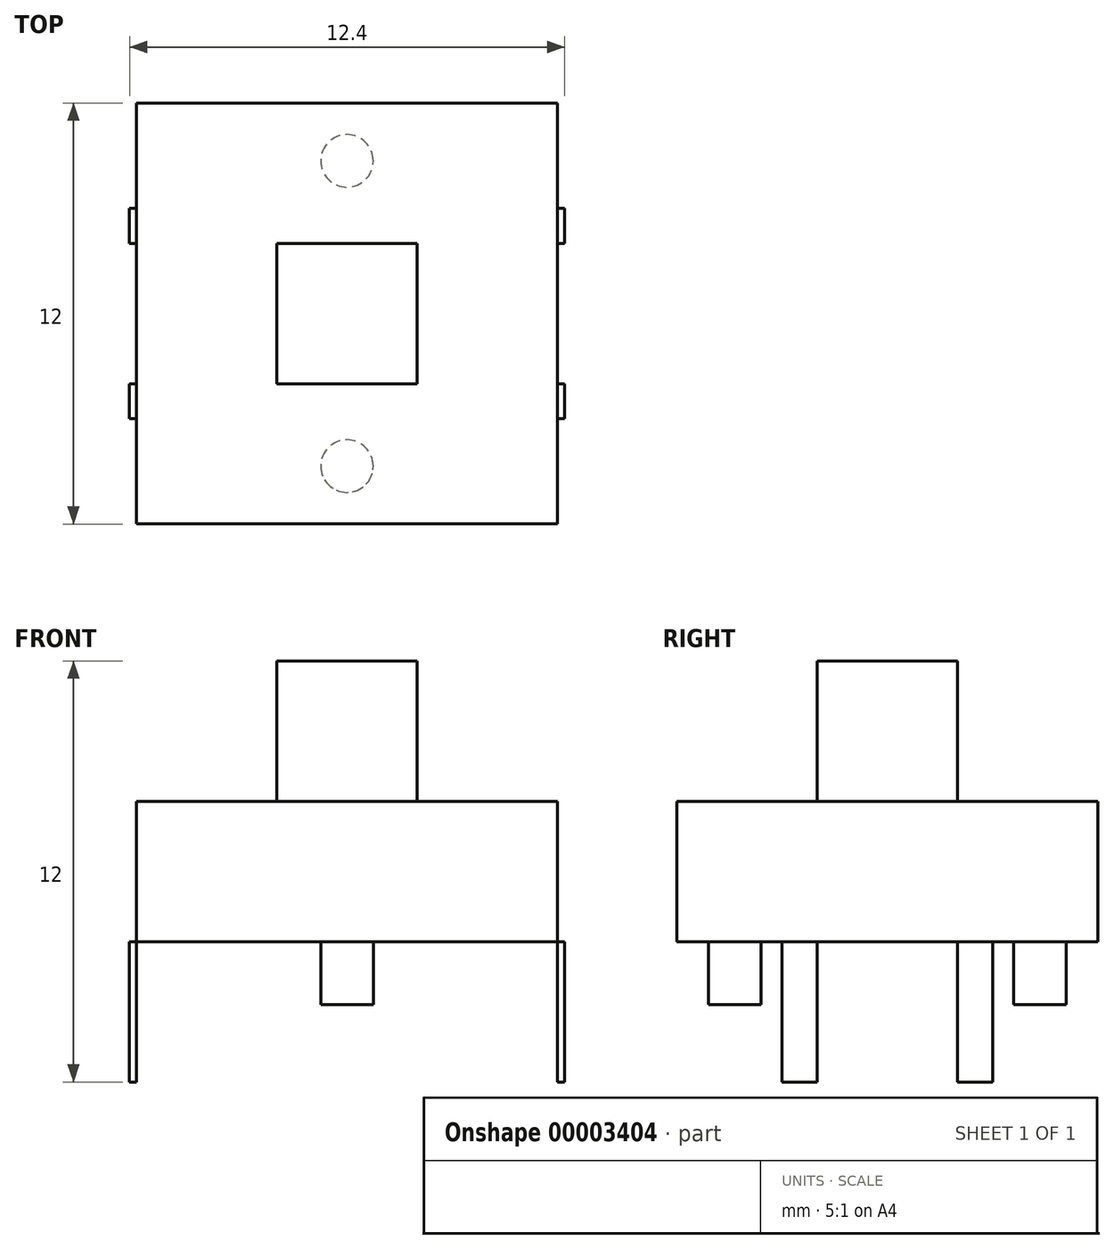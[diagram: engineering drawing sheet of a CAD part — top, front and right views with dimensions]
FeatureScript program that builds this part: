
annotation { "Feature Type Name" : "Feature", "Feature Type Description" : "" }
export const myFeature = defineFeature(function(context is Context, id is Id, definition is map)
    precondition{}
    {
        {
            var Q0;
            Q0=qCreatedBy(makeId("Top.planeOp"),FACE);
            var sketch = newSketch(context, id + "F0", { "sketchPlane" : qUnion([Q0])});
            skLineSegment(sketch, "E0.bottom", {"start": v(-5.22, 9.33) * mm, "end": v(6.78, 9.33) * mm});
            skLineSegment(sketch, "E0.top", {"start": v(-5.22, -2.67) * mm, "end": v(6.78, -2.67) * mm});
            skLineSegment(sketch, "E0.left", {"start": v(-5.22, 9.33) * mm, "end": v(-5.22, -2.67) * mm});
            skLineSegment(sketch, "E0.right", {"start": v(6.78, 9.33) * mm, "end": v(6.78, -2.67) * mm});
            skSolve(sketch);
        }
        {
            var Q0;
            Q0=makeQuery(id+"F0.imprint","IMPRINT",FACE,{"disambiguationData":[TD([[makeQuery(id+"F0.imprint","IMPRINT",EDGE,{"derivedFrom":sQuery(id+"F0.wireOp",EDGE,"E0.bottom")}),-1.0]])]});
            extrude(context, id + "F1", {"entities" : qUnion([Q0]), "depth" : 4 * mm});
        }
        {
            var Q0;
            Q0=makeQuery(id+"F1.opExtrude","CAP_FACE",FACE,{"disambiguationData":[OSD([sQuery(id+"F0.wireOp",EDGE,"E0.bottom"),sQuery(id+"F0.wireOp",EDGE,"E0.top"),sQuery(id+"F0.wireOp",EDGE,"E0.left"),sQuery(id+"F0.wireOp",EDGE,"E0.right")])],"isStart":false});
            var sketch = newSketch(context, id + "F2", { "sketchPlane" : qUnion([Q0])});
            skLineSegment(sketch, "E1.0.0", {"start": v(-5.22, 9.33) * mm, "end": v(6.78, 9.33) * mm});
            skLineSegment(sketch, "E1.0.1", {"start": v(-5.22, 9.33) * mm, "end": v(-5.22, -2.67) * mm});
            skLineSegment(sketch, "E1.0.2", {"start": v(-5.22, -2.67) * mm, "end": v(6.78, -2.67) * mm});
            skLineSegment(sketch, "E1.0.3", {"start": v(6.78, 9.33) * mm, "end": v(6.78, -2.67) * mm});
            skLineSegment(sketch, "E2.0", {"start": v(-1.22, 5.33) * mm, "end": v(2.78, 5.33) * mm});
            skLineSegment(sketch, "E2.1", {"start": v(-1.22, 5.33) * mm, "end": v(-1.22, 1.33) * mm});
            skLineSegment(sketch, "E2.2", {"start": v(-1.22, 1.33) * mm, "end": v(2.78, 1.33) * mm});
            skLineSegment(sketch, "E2.3", {"start": v(2.78, 5.33) * mm, "end": v(2.78, 1.33) * mm});
            skSolve(sketch);
        }
        {
            var Q0;
            Q0=makeQuery(id+"F2.imprint","IMPRINT",FACE,{"disambiguationData":[TD([[makeQuery(id+"F2.imprint","IMPRINT",EDGE,{"derivedFrom":sQuery(id+"F2.wireOp",EDGE,"E2.0")}),-1.0]])]});
            extrude(context, id + "F3", {"entities" : qUnion([Q0]), "operationType" : NewBodyOperationType.ADD, "depth" : 4 * mm});
        }
        {
            var Q0;
            Q0=makeQuery(id+"F1.opExtrude","CAP_FACE",FACE,{"disambiguationData":[OSD([sQuery(id+"F0.wireOp",EDGE,"E0.bottom"),sQuery(id+"F0.wireOp",EDGE,"E0.top"),sQuery(id+"F0.wireOp",EDGE,"E0.left"),sQuery(id+"F0.wireOp",EDGE,"E0.right")])],"isStart":true});
            var sketch = newSketch(context, id + "F4", { "sketchPlane" : qUnion([Q0])});
            skLineSegment(sketch, "E3.bottom", {"start": v(6.98, -0.33) * mm, "end": v(6.78, -0.33) * mm});
            skLineSegment(sketch, "E3.top", {"start": v(6.98, -1.33) * mm, "end": v(6.78, -1.33) * mm});
            skLineSegment(sketch, "E3.left", {"start": v(6.78, -0.33) * mm, "end": v(6.78, -1.33) * mm});
            skLineSegment(sketch, "E3.right", {"start": v(6.98, -0.33) * mm, "end": v(6.98, -1.33) * mm});
            skLineSegment(sketch, "E4.bottom", {"start": v(6.78, -6.33) * mm, "end": v(6.98, -6.33) * mm});
            skLineSegment(sketch, "E4.top", {"start": v(6.78, -5.33) * mm, "end": v(6.98, -5.33) * mm});
            skLineSegment(sketch, "E4.left", {"start": v(6.78, -6.33) * mm, "end": v(6.78, -5.33) * mm});
            skLineSegment(sketch, "E4.right", {"start": v(6.98, -6.33) * mm, "end": v(6.98, -5.33) * mm});
            skLineSegment(sketch, "E5.bottom", {"start": v(-5.22, -0.33) * mm, "end": v(-5.42, -0.33) * mm});
            skLineSegment(sketch, "E5.top", {"start": v(-5.22, -1.33) * mm, "end": v(-5.42, -1.33) * mm});
            skLineSegment(sketch, "E5.left", {"start": v(-5.22, -0.33) * mm, "end": v(-5.22, -1.33) * mm});
            skLineSegment(sketch, "E5.right", {"start": v(-5.42, -0.33) * mm, "end": v(-5.42, -1.33) * mm});
            skLineSegment(sketch, "E6.bottom", {"start": v(-5.22, -5.33) * mm, "end": v(-5.42, -5.33) * mm});
            skLineSegment(sketch, "E6.top", {"start": v(-5.22, -6.33) * mm, "end": v(-5.42, -6.33) * mm});
            skLineSegment(sketch, "E6.left", {"start": v(-5.22, -5.33) * mm, "end": v(-5.22, -6.33) * mm});
            skLineSegment(sketch, "E6.right", {"start": v(-5.42, -5.33) * mm, "end": v(-5.42, -6.33) * mm});
            skLineSegment(sketch, "E7.0.0", {"start": v(-5.22, -9.33) * mm, "end": v(6.78, -9.33) * mm});
            skLineSegment(sketch, "E7.0.1", {"start": v(6.78, -9.33) * mm, "end": v(6.78, 2.67) * mm});
            skLineSegment(sketch, "E7.0.2", {"start": v(-5.22, 2.67) * mm, "end": v(6.78, 2.67) * mm});
            skLineSegment(sketch, "E7.0.3", {"start": v(-5.22, -9.33) * mm, "end": v(-5.22, 2.67) * mm});
            skSolve(sketch);
        }
        {
            var Q0;
            {var subQ2=sQuery(id+"F4.wireOp",EDGE,"E3.bottom");Q0=makeQuery(id+"F4.imprint","IMPRINT",FACE,{"disambiguationData":[TD([[makeQuery(id+"F4.imprint","IMPRINT",EDGE,{"derivedFrom":subQ2}),1.0]])]});}
            var Q1;
            {var subQ2=sQuery(id+"F4.wireOp",EDGE,"E5.bottom");Q1=makeQuery(id+"F4.imprint","IMPRINT",FACE,{"disambiguationData":[TD([[makeQuery(id+"F4.imprint","IMPRINT",EDGE,{"derivedFrom":subQ2}),1.0]])]});}
            var Q2;
            {var subQ2=sQuery(id+"F4.wireOp",EDGE,"E6.bottom");Q2=makeQuery(id+"F4.imprint","IMPRINT",FACE,{"disambiguationData":[TD([[makeQuery(id+"F4.imprint","IMPRINT",EDGE,{"derivedFrom":subQ2}),1.0]])]});}
            var Q3;
            {var subQ2=sQuery(id+"F4.wireOp",EDGE,"E4.bottom");Q3=makeQuery(id+"F4.imprint","IMPRINT",FACE,{"disambiguationData":[TD([[makeQuery(id+"F4.imprint","IMPRINT",EDGE,{"derivedFrom":subQ2}),1.0]])]});}
            extrude(context, id + "F5", {"entities" : qUnion([Q0, Q1, Q2, Q3]), "depth" : 4 * mm});
        }
        {
            var Q0;
            Q0=makeQuery(id+"F1.opExtrude","CAP_FACE",FACE,{"disambiguationData":[OSD([sQuery(id+"F0.wireOp",EDGE,"E0.bottom"),sQuery(id+"F0.wireOp",EDGE,"E0.top"),sQuery(id+"F0.wireOp",EDGE,"E0.left"),sQuery(id+"F0.wireOp",EDGE,"E0.right")])],"isStart":true});
            var sketch = newSketch(context, id + "F6", { "sketchPlane" : qUnion([Q0])});
            skLineSegment(sketch, "E8", {"start": v(0.78, -9.33) * mm, "end": v(0.78, 2.67) * mm, "construction": true});
            skCircle(sketch, "E9", {"center": v(0.78, -7.68) * mm, "radius": 0.75 * mm});
            skCircle(sketch, "E10", {"center": v(0.78, 1.02) * mm, "radius": 0.75 * mm});
            skSolve(sketch);
        }
        {
            var Q0;
            Q0=makeQuery(id+"F6.imprint","IMPRINT",FACE,{"disambiguationData":[TD([[makeQuery(id+"F6.imprint","IMPRINT",EDGE,{"derivedFrom":sQuery(id+"F6.wireOp",EDGE,"E9")}),1.0]])]});
            var Q1;
            Q1=makeQuery(id+"F6.imprint","IMPRINT",FACE,{"disambiguationData":[TD([[makeQuery(id+"F6.imprint","IMPRINT",EDGE,{"derivedFrom":sQuery(id+"F6.wireOp",EDGE,"E10")}),1.0]])]});
            extrude(context, id + "F7", {"entities" : qUnion([Q0, Q1]), "operationType" : NewBodyOperationType.ADD, "depth" : 1.8 * mm});
        }
    });
